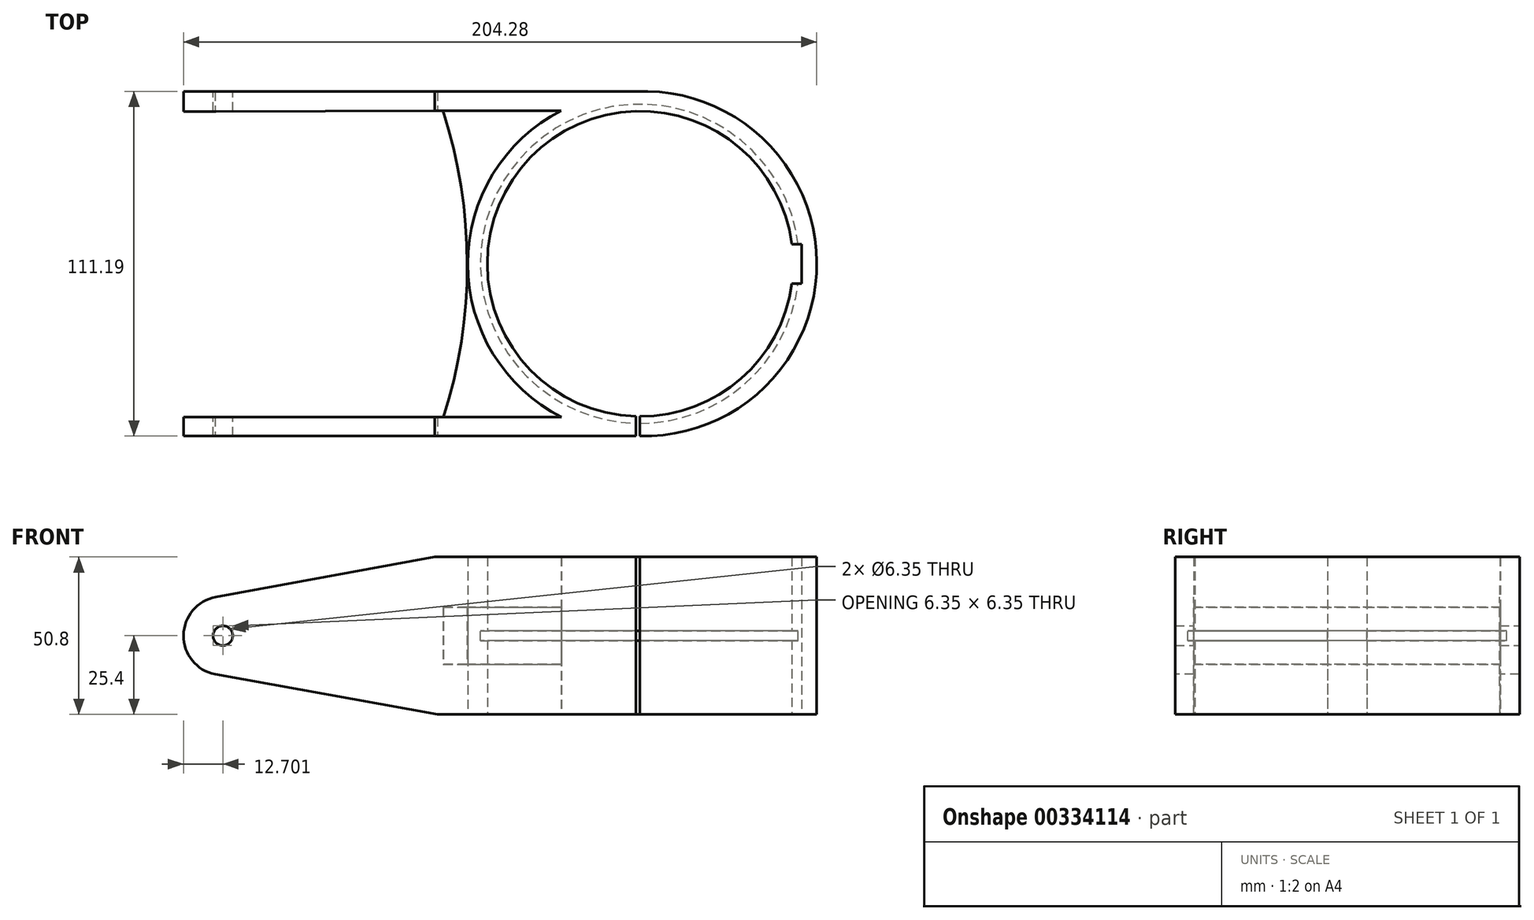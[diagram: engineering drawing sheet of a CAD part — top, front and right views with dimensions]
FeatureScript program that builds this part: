
annotation { "Feature Type Name" : "Feature", "Feature Type Description" : "" }
export const myFeature = defineFeature(function(context is Context, id is Id, definition is map)
    precondition{}
    {
        {
            var Q0;
            Q0=qCreatedBy(makeId("Top.planeOp"),FACE);
            var sketch = newSketch(context, id + "F0", { "sketchPlane" : qUnion([Q0])});
            skArc(sketch, "E0", {"start": v(0, -49.21) * mm, "mid": v(0.63, 49.2) * mm, "end": v(-1.27, -49.2) * mm});
            skArc(sketch, "E1.0", {"start": v(-25.41, 49.4) * mm, "mid": v(-55.56, -0.1) * mm, "end": v(-25.23, -49.5) * mm});
            skLineSegment(sketch, "E2", {"start": v(-1.27, 55.55) * mm, "end": v(-1.27, 49.2) * mm});
            skLineSegment(sketch, "E3", {"start": v(0, -49.21) * mm, "end": v(0, -55.56) * mm});
            skLineSegment(sketch, "E4.bottom", {"start": v(-1.27, 55.55) * mm, "end": v(-147.32, 55.55) * mm});
            skLineSegment(sketch, "E4.top", {"start": v(-1.27, -55.58) * mm, "end": v(-147.32, -55.58) * mm});
            skLineSegment(sketch, "E5.trimOffspring", {"start": v(-1.27, -49.2) * mm, "end": v(-1.27, -55.58) * mm});
            skLineSegment(sketch, "E6", {"start": v(-147.32, 55.55) * mm, "end": v(-147.32, 49.1) * mm});
            skLineSegment(sketch, "E7", {"start": v(-147.32, -55.58) * mm, "end": v(-147.32, -49.5) * mm});
            skLineSegment(sketch, "E8", {"start": v(-147.32, -49.5) * mm, "end": v(-25.23, -49.5) * mm});
            skLineSegment(sketch, "E9", {"start": v(-147.32, 49.1) * mm, "end": v(-25.41, 49.4) * mm});
            skArc(sketch, "E10", {"start": v(-63.33, -49.5) * mm, "mid": v(-55.7, -0.03) * mm, "end": v(-63.51, 49.4) * mm});
            skLineSegment(sketch, "E11", {"start": v(-69.68, -49.5) * mm, "end": v(-63.33, -49.5) * mm});
            skArc(sketch, "E12", {"start": v(0, -55.56) * mm, "mid": v(57.05, 0.65) * mm, "end": v(-1.27, 55.55) * mm});
            skArc(sketch, "E13", {"start": v(0, -49.21) * mm, "mid": v(49.45, 0.64) * mm, "end": v(-1.27, 49.2) * mm});
            skLineSegment(sketch, "E14", {"start": v(49.04, 6.35) * mm, "end": v(52.21, 6.35) * mm});
            skLineSegment(sketch, "E15", {"start": v(52.21, 6.35) * mm, "end": v(52.21, -6.35) * mm});
            skLineSegment(sketch, "E16", {"start": v(52.21, -6.35) * mm, "end": v(49.04, -6.35) * mm});
            skSolve(sketch);
        }
        {
            var Q0;
            {var subQ3=sQuery(id+"F0.wireOp",EDGE,"E4.bottom");Q0=makeQuery(id+"F0.imprint","IMPRINT",FACE,{"disambiguationData":[TD([[makeQuery(id+"F0.imprint","IMPRINT",EDGE,{"derivedFrom":subQ3}),1.0]])]});}
            var Q1;
            {var subQ2=sQuery(id+"F0.wireOp",EDGE,"E4.top");Q1=makeQuery(id+"F0.imprint","IMPRINT",FACE,{"disambiguationData":[TD([[makeQuery(id+"F0.imprint","IMPRINT",EDGE,{"derivedFrom":subQ2}),-1.0]])]});}
            var Q2;
            {var subQ4=sQuery(id+"F0.wireOp",EDGE,"E2");Q2=makeQuery(id+"F0.imprint","IMPRINT",FACE,{"disambiguationData":[TD([[makeQuery(id+"F0.imprint","IMPRINT",EDGE,{"derivedFrom":subQ4}),-1.0]])]});}
            extrude(context, id + "F1", {"entities" : qUnion([Q0, Q1, Q2]), "endBound" : BoundingType.SYMMETRIC, "depth" : 50.8 * mm});
        }
        {
            var Q0;
            Q0=makeQuery(id+"F1.opExtrude","SWEPT_FACE",FACE,{"disambiguationData":[OSD([sQuery(id+"F0.wireOp",EDGE,"E4.top")])]});
            var sketch = newSketch(context, id + "F2", { "sketchPlane" : qUnion([Q0])});
            skSolve(sketch);
        }
        {
            var Q0;
            {var subQ0=sQuery(id+"F0.wireOp",EDGE,"E1.0");Q0=makeQuery(id+"F0.imprint","IMPRINT",FACE,{"disambiguationData":[TD([[makeQuery(id+"F0.imprint","IMPRINT",EDGE,{"derivedFrom":subQ0}),-1.0]])]});}
            var Q1;
            Q1=sQuery(id+"F0.wireOp",EDGE,"E11");
            var Q2;
            Q2=sQuery(id+"F0.wireOp",EDGE,"E10");
            var Q3;
            Q3=sQuery(id+"F0.wireOp",EDGE,"rBlO6ro3-5g2z-FfBw-8hij-tyMhMfmKPz8U");
            var Q4;
            Q4=sQuery(id+"F0.wireOp",EDGE,"kr6a58jN-BYY1-x4jS-eH9u-tcZzHDnncJ3J");
            extrude(context, id + "F3", {"entities" : qUnion([Q0]), "surfaceEntities" : qUnion([Q1, Q2, Q3, Q4]), "endBound" : BoundingType.SYMMETRIC, "depth" : 18.41 * mm});
        }
        {
            var Q0;
            Q0=makeQuery(id+"F0.imprint","IMPRINT",FACE,{"disambiguationData":[TD([[makeQuery(id+"F0.imprint","IMPRINT",EDGE,{"derivedFrom":sQuery(id+"F0.wireOp",EDGE,"E12")}),1.0]])]});
            extrude(context, id + "F4", {"entities" : qUnion([Q0]), "operationType" : NewBodyOperationType.ADD, "endBound" : BoundingType.SYMMETRIC, "depth" : 50.8 * mm});
        }
        {
            var Q0;
            {var subQ0=sQuery(id+"F0.wireOp",EDGE,"E4.top");Q0=makeQuery(id+"F2.imprint","IMPRINT",FACE,{"disambiguationData":[TD([[makeQuery(id+"F2.imprint","IMPRINT",EDGE,{"derivedFrom":makeQuery(id+"F1.opExtrude","CAP_EDGE",EDGE,{"disambiguationData":[OSD([subQ0])],"isStart":true})}),-1.0]])]});}
            var sketch = newSketch(context, id + "F5", { "sketchPlane" : qUnion([Q0])});
            skArc(sketch, "E17", {"start": v(-136.8, 12.5) * mm, "mid": v(-147.22, 0.14) * mm, "end": v(-137.07, -12.44) * mm});
            skLineSegment(sketch, "E18", {"start": v(-136.8, 12.5) * mm, "end": v(-64.67, 25.67) * mm});
            skLineSegment(sketch, "E19.bottom", {"start": v(-147.4, -25.5) * mm, "end": v(-64.67, -25.5) * mm});
            skLineSegment(sketch, "E19.top", {"start": v(-147.4, 25.67) * mm, "end": v(-64.67, 25.67) * mm});
            skLineSegment(sketch, "E19.left", {"start": v(-147.4, -25.5) * mm, "end": v(-147.4, 25.67) * mm});
            skLineSegment(sketch, "E19.right", {"start": v(-64.67, -25.5) * mm, "end": v(-64.67, 25.67) * mm});
            skLineSegment(sketch, "E20", {"start": v(-137.07, -12.44) * mm, "end": v(-64.67, -25.5) * mm});
            skSolve(sketch);
        }
        {
            var Q0;
            {var subQ3=sQuery(id+"F5.wireOp",EDGE,"E17");Q0=makeQuery(id+"F5.imprint","IMPRINT",FACE,{"disambiguationData":[TD([[makeQuery(id+"F5.imprint","IMPRINT",EDGE,{"derivedFrom":subQ3}),-1.0]])]});}
            extrude(context, id + "F6", {"entities" : qUnion([Q0]), "operationType" : NewBodyOperationType.REMOVE, "depth" : -120.65 * mm});
        }
        {
            var Q0;
            Q0=makeQuery(id+"F1.opExtrude","SWEPT_FACE",FACE,{"disambiguationData":[OSD([sQuery(id+"F0.wireOp",EDGE,"E4.bottom")])]});
            var sketch = newSketch(context, id + "F7", { "sketchPlane" : qUnion([Q0])});
            skCircle(sketch, "E21", {"center": v(134.52, 0) * mm, "radius": 3.17 * mm});
            skSolve(sketch);
        }
        {
            var Q0;
            Q0=qSketchRegion(id+"F7",true);
            extrude(context, id + "F8", {"entities" : qUnion([Q0]), "operationType" : NewBodyOperationType.REMOVE, "oppositeDirection" : true, "depth" : 114.3 * mm});
        }
        {
            var Q0;
            Q0=qCreatedBy(makeId("Top.planeOp"),FACE);
            var sketch = newSketch(context, id + "F9", { "sketchPlane" : qUnion([Q0])});
            skCircle(sketch, "E22", {"center": v(0, 0) * mm, "radius": 51.46 * mm});
            skSolve(sketch);
        }
        {
            var Q0;
            Q0=qSketchRegion(id+"F9",true);
            extrude(context, id + "F10", {"entities" : qUnion([Q0]), "operationType" : NewBodyOperationType.REMOVE, "endBound" : BoundingType.SYMMETRIC, "oppositeDirection" : true, "depth" : 3.17 * mm});
        }
    });
